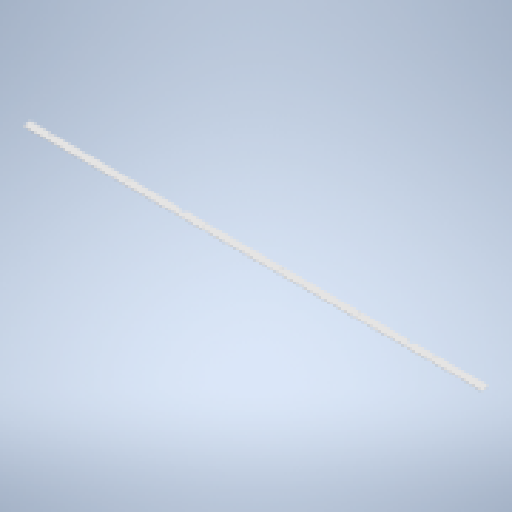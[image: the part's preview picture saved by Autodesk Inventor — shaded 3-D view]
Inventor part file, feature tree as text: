
AUTODESK INVENTOR PART (.ipt)
format: ipt  version: 2025 (Build 290162010, 162A)  size: 346,112 bytes
history: native  units: mm
features: sketch x4, other x3, extrude x2, sheet_metal_op x1, pattern_linear x1, projected_geometry x1
ambient origin geometry x8: Origin, YZ Plane, XZ Plane, XY Plane, X Axis, Y Axis, Z Axis, Center Point
bodies: Body1 (feature_tree)
feature tree (12):
  sheet_metal_op  "Face3"
  extrude  "Extrusion3"  Depth=2980.0mm
  pattern_linear  "Rectangular Pattern2"  Spacing1=26.0mm  [1 undecoded]
  extrude  "Extrusion4"  TaperAngle=0.0deg  [1 undecoded]
  other  "Mark1"
  sketch  "Sketch8"  dims[d37=50.0mm d38=2980.0mm]
  other  "Plate5"
  sketch  "Sketch9"  dims[d41=3.0mm]
  sketch  "Sketch10"  dims[d42=293.0mm]
  projected_geometry  "Projected Loop2"
  sketch  "Sketch11"  dims[d43=3.2mm d44=26.0mm d45=0.0mm d46=0.0mm d47=60.0mm d49=500.0mm d50=40.0mm d51=1480.0mm d52=1000.0mm d53=0.0mm d54=0.0mm]
  other  "Definition1"
note: 2 required parameter values undecoded (feature->parameter linkage not recoverable at this tier; creation-order binding heuristic only, values carry confidence <= 0.55)
